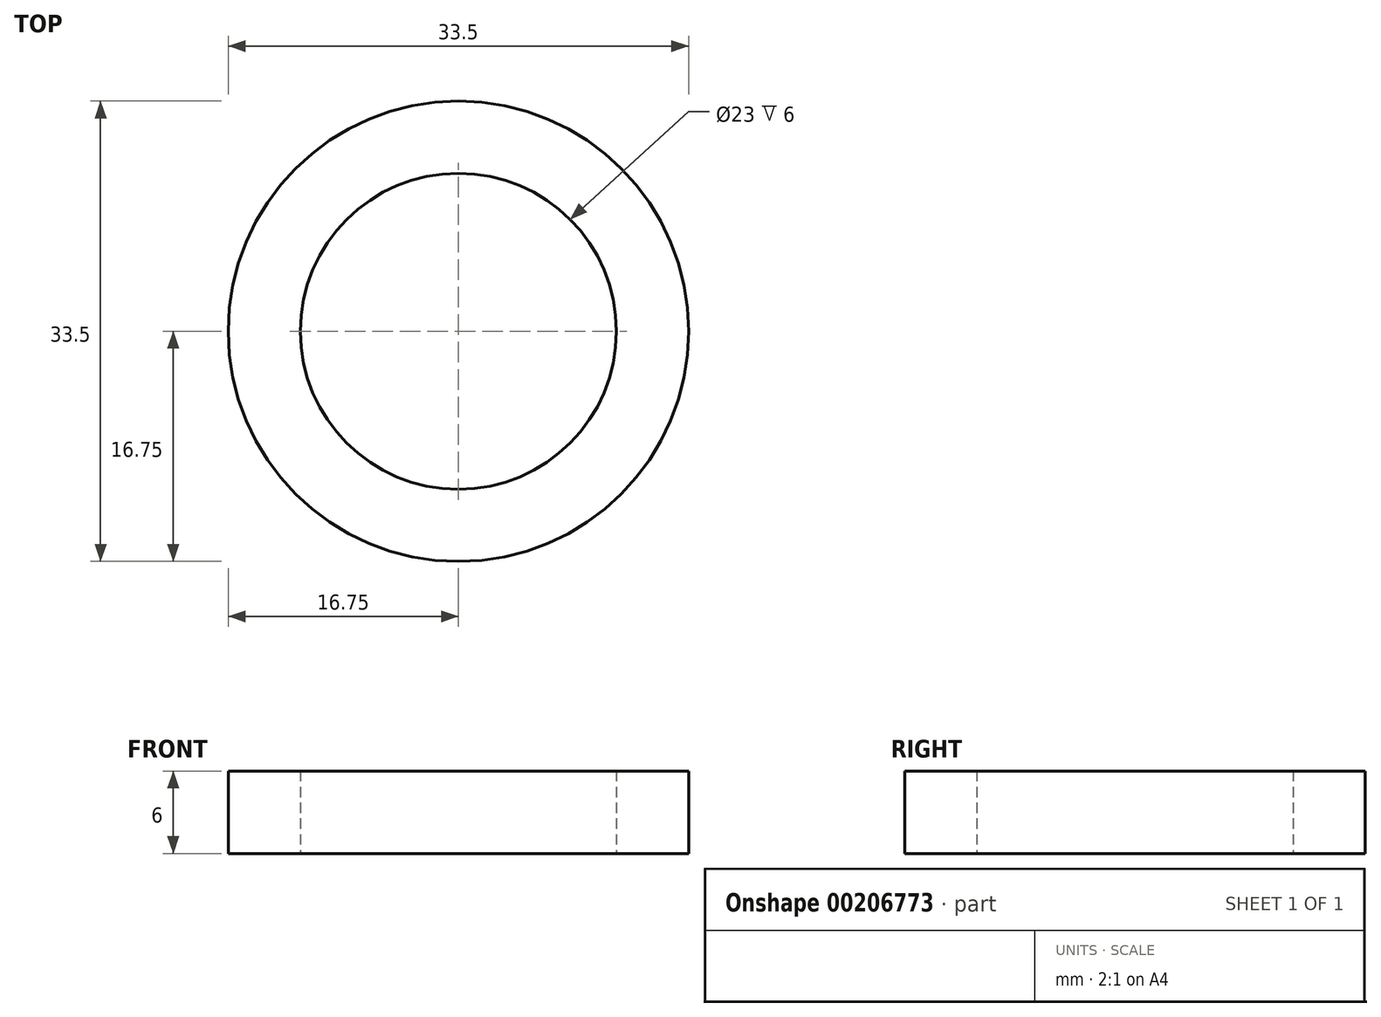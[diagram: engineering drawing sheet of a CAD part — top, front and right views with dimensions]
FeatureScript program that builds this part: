
annotation { "Feature Type Name" : "Feature", "Feature Type Description" : "" }
export const myFeature = defineFeature(function(context is Context, id is Id, definition is map)
    precondition{}
    {
        {
            var Q0;
            Q0=qCreatedBy(makeId("Top.planeOp"),FACE);
            var sketch = newSketch(context, id + "F0", { "sketchPlane" : qUnion([Q0])});
            skCircle(sketch, "E0", {"center": v(0, 0) * mm, "radius": 16.75 * mm});
            skCircle(sketch, "E1", {"center": v(0, 0) * mm, "radius": 11.5 * mm});
            skSolve(sketch);
        }
        {
            var Q0;
            Q0=makeQuery(id+"F0.imprint","IMPRINT",FACE,{"disambiguationData":[TD([[makeQuery(id+"F0.imprint","IMPRINT",EDGE,{"derivedFrom":sQuery(id+"F0.wireOp",EDGE,"E0")}),1.0]])]});
            extrude(context, id + "F1", {"entities" : qUnion([Q0]), "depth" : 6 * mm, "offsetDistance" : 25 * mm});
        }
    });
